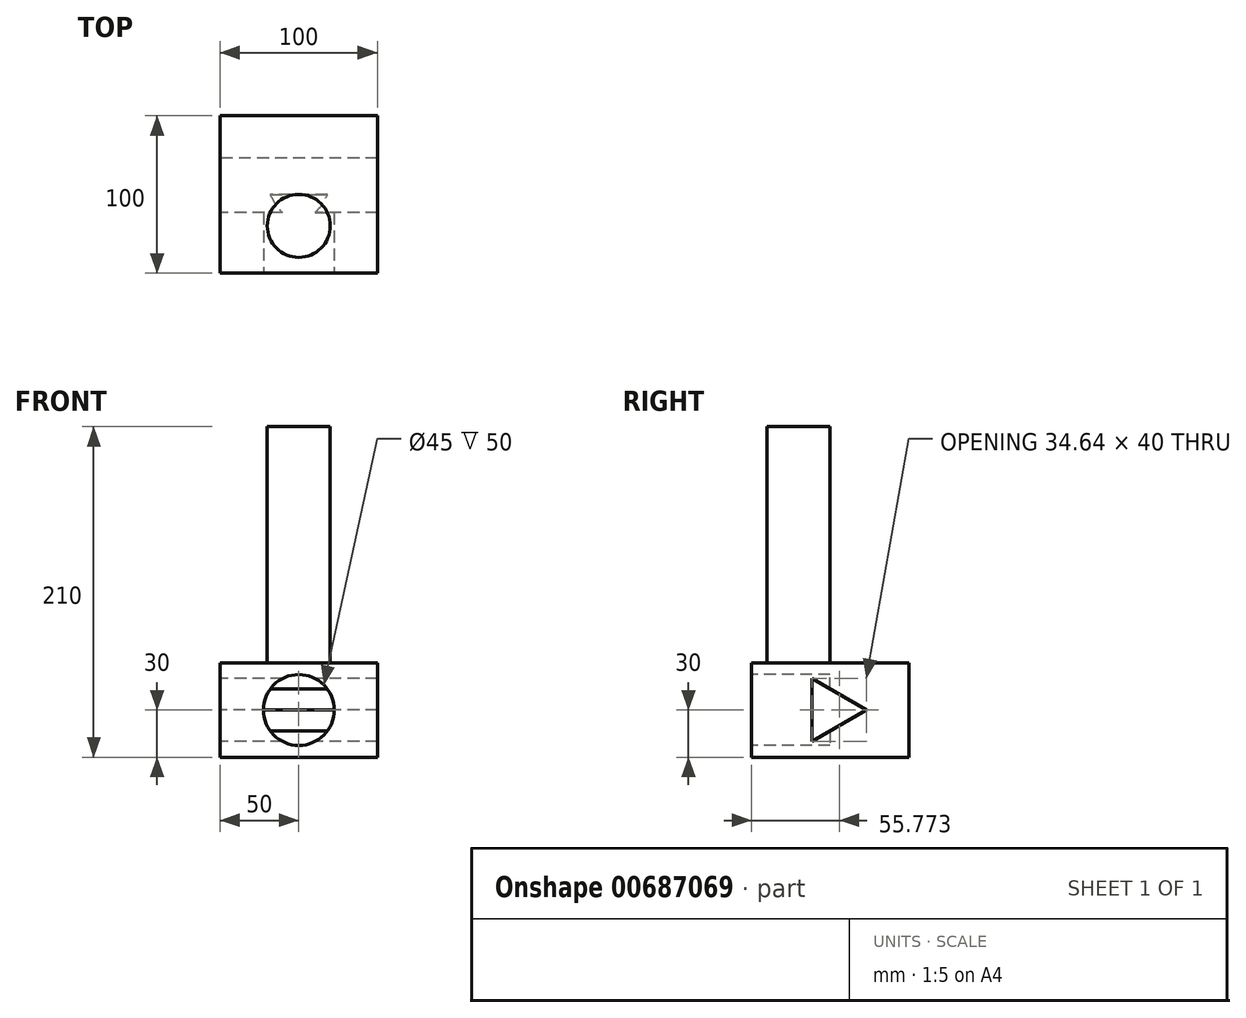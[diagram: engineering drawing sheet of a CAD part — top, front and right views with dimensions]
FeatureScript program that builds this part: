
annotation { "Feature Type Name" : "Feature", "Feature Type Description" : "" }
export const myFeature = defineFeature(function(context is Context, id is Id, definition is map)
    precondition{}
    {
        {
            var Q0;
            Q0=qCreatedBy(makeId("Top.planeOp"),FACE);
            var sketch = newSketch(context, id + "F0", { "sketchPlane" : qUnion([Q0])});
            skLineSegment(sketch, "E0.bottom", {"start": v(50, 50) * mm, "end": v(-50, 50) * mm});
            skLineSegment(sketch, "E0.top", {"start": v(50, -50) * mm, "end": v(-50, -50) * mm});
            skLineSegment(sketch, "E0.left", {"start": v(50, 50) * mm, "end": v(50, -50) * mm});
            skLineSegment(sketch, "E0.right", {"start": v(-50, 50) * mm, "end": v(-50, -50) * mm});
            skPoint(sketch, "E0.middle", {"position": v(0, 0) * mm});
            skSolve(sketch);
        }
        {
            var Q0;
            Q0 = qSketchRegion(id + "F0", true);
            extrude(context, id + "F1", {"entities" : qUnion([Q0]), "depth" : 60 * mm, "offsetDistance" : 25 * mm});
        }
        {
            var Q0;
            Q0=makeQuery(id+"F1.opExtrude","CAP_FACE",FACE,{"disambiguationData":[OSD([sQuery(id+"F0.wireOp",EDGE,"E0.bottom"),sQuery(id+"F0.wireOp",EDGE,"E0.top"),sQuery(id+"F0.wireOp",EDGE,"E0.left"),sQuery(id+"F0.wireOp",EDGE,"E0.right")])],"isStart":false});
            var sketch = newSketch(context, id + "F2", { "sketchPlane" : qUnion([Q0])});
            skCircle(sketch, "E1", {"center": v(0, -20) * mm, "radius": 20 * mm});
            skPoint(sketch, "E1.first.point", {"position": v(0, 0) * mm});
            skPoint(sketch, "E1.second.point", {"position": v(0, -40) * mm});
            skPoint(sketch, "E1.third.point", {"position": v(20, -20) * mm});
            skSolve(sketch);
        }
        {
            var Q0;
            Q0 = qSketchRegion(id + "F2", true);
            extrude(context, id + "F3", {"entities" : qUnion([Q0]), "operationType" : NewBodyOperationType.ADD, "depth" : 150 * mm, "offsetDistance" : 25 * mm});
        }
        {
            var Q0;
            Q0=makeQuery(id+"F1.opExtrude","SWEPT_FACE",FACE,{"disambiguationData":[OSD([sQuery(id+"F0.wireOp",EDGE,"E0.right")])]});
            var sketch = newSketch(context, id + "F4", { "sketchPlane" : qUnion([Q0])});
            skCircle(sketch, "E2.cCircle", {"center": v(0, 30) * mm, "radius": 11.55 * mm, "construction": true});
            skLineSegment(sketch, "E2.0", {"start": v(11.55, 10) * mm, "end": v(-23.1, 30) * mm});
            skLineSegment(sketch, "E2.1", {"start": v(-23.1, 30) * mm, "end": v(11.55, 50) * mm});
            skLineSegment(sketch, "E2.2", {"start": v(11.55, 50) * mm, "end": v(11.55, 10) * mm});
            skPoint(sketch, "E2.0.midPoint", {"position": v(-5.77, 20) * mm});
            skSolve(sketch);
        }
        {
            var Q0;
            Q0 = qSketchRegion(id + "F4", true);
            extrude(context, id + "F5", {"entities" : qUnion([Q0]), "operationType" : NewBodyOperationType.REMOVE, "oppositeDirection" : true, "depth" : 100 * mm, "offsetDistance" : 25 * mm});
        }
        {
            var Q0;
            Q0=makeQuery(id+"F1.opExtrude","SWEPT_FACE",FACE,{"disambiguationData":[OSD([sQuery(id+"F0.wireOp",EDGE,"E0.top")])]});
            var sketch = newSketch(context, id + "F6", { "sketchPlane" : qUnion([Q0])});
            skCircle(sketch, "E3", {"center": v(0, 30) * mm, "radius": 22.5 * mm});
            skSolve(sketch);
        }
        {
            var Q0;
            Q0 = qSketchRegion(id + "F6", true);
            extrude(context, id + "F7", {"entities" : qUnion([Q0]), "operationType" : NewBodyOperationType.REMOVE, "oppositeDirection" : true, "depth" : 50 * mm, "offsetDistance" : 25 * mm});
        }
    });
